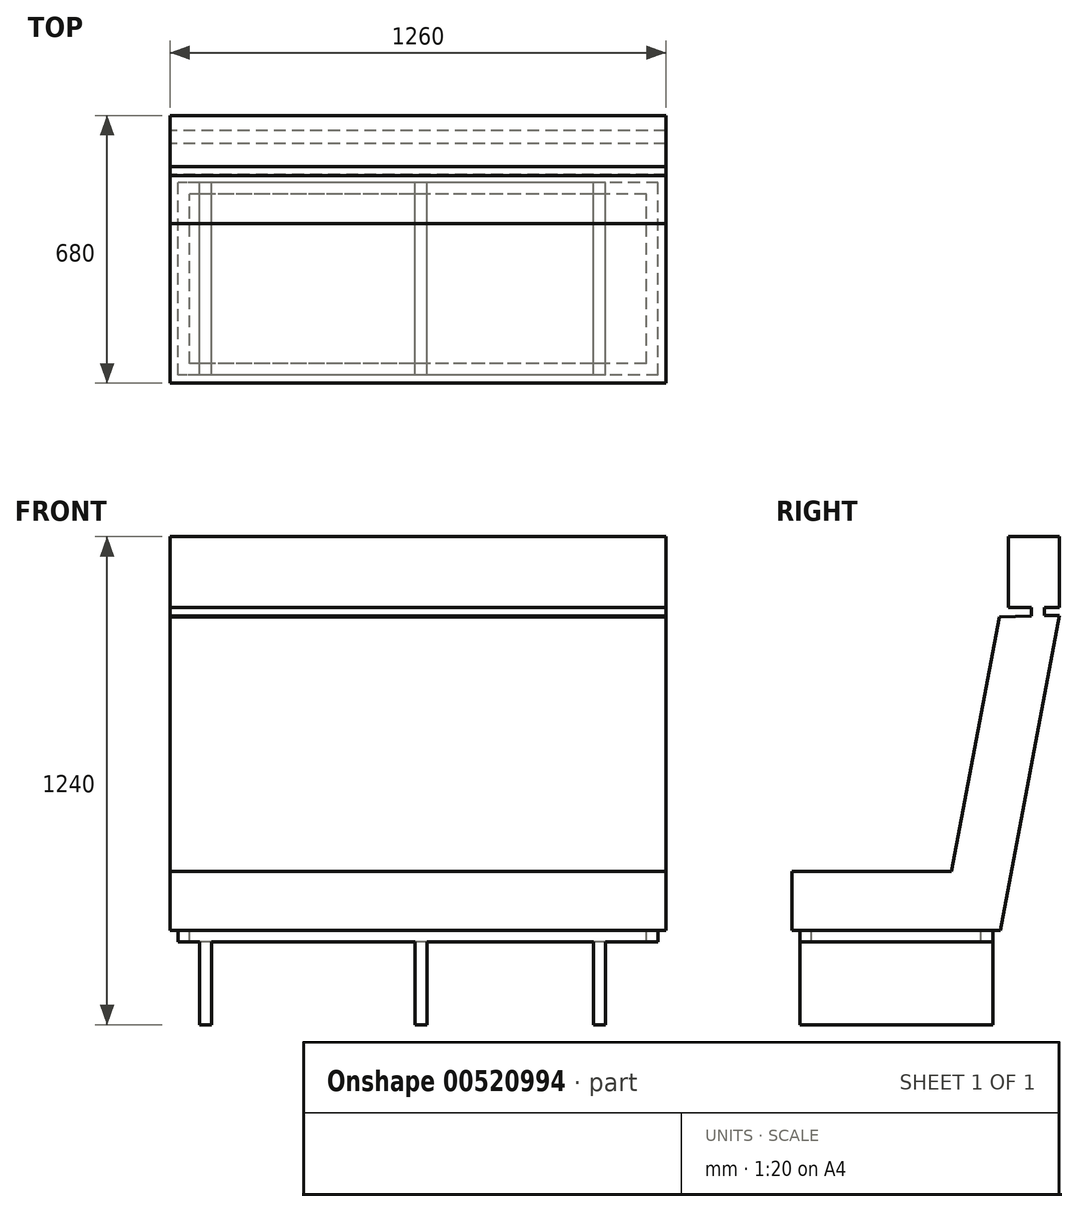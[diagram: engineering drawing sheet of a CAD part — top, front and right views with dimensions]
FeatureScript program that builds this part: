
annotation { "Feature Type Name" : "Feature", "Feature Type Description" : "" }
export const myFeature = defineFeature(function(context is Context, id is Id, definition is map)
    precondition{}
    {
        {
            var Q0;
            Q0=qCreatedBy(makeId("Right.planeOp"),FACE);
            var sketch = newSketch(context, id + "F0", { "sketchPlane" : qUnion([Q0])});
            skLineSegment(sketch, "E0", {"start": v(0, 0) * mm, "end": v(0, 800) * mm, "construction": true});
            skLineSegment(sketch, "E1", {"start": v(0, 0) * mm, "end": v(-150, 0) * mm, "construction": true});
            skLineSegment(sketch, "E2", {"start": v(-150, 0) * mm, "end": v(0, 800) * mm});
            skLineSegment(sketch, "E3", {"start": v(-150, 0) * mm, "end": v(-680, 0) * mm});
            skLineSegment(sketch, "E4.0", {"start": v(-274.49, 150) * mm, "end": v(-153.31, 796.27) * mm});
            skLineSegment(sketch, "E4.1", {"start": v(-274.49, 150) * mm, "end": v(-680, 150) * mm});
            skLineSegment(sketch, "E5", {"start": v(-680, 0) * mm, "end": v(-680, 150) * mm});
            skLineSegment(sketch, "E6", {"start": v(0, 800) * mm, "end": v(-38.22, 799.07) * mm});
            skLineSegment(sketch, "E7.bottom", {"start": v(0, 820) * mm, "end": v(-38.22, 820) * mm});
            skLineSegment(sketch, "E7.top", {"start": v(0, 1000) * mm, "end": v(-130, 1000) * mm});
            skLineSegment(sketch, "E7.left", {"start": v(0, 820) * mm, "end": v(0, 1000) * mm});
            skLineSegment(sketch, "E7.right", {"start": v(-130, 820) * mm, "end": v(-130, 1000) * mm});
            skLineSegment(sketch, "E8", {"start": v(-38.22, 820) * mm, "end": v(-38.22, 799.07) * mm});
            skLineSegment(sketch, "E9", {"start": v(-71.85, 798.25) * mm, "end": v(-71.85, 820) * mm});
            skLineSegment(sketch, "E10.trimOffspring", {"start": v(-71.85, 798.25) * mm, "end": v(-153.31, 796.27) * mm});
            skLineSegment(sketch, "E11.trimOffspring", {"start": v(-71.85, 820) * mm, "end": v(-130, 820) * mm});
            skSolve(sketch);
        }
        {
            var Q0;
            Q0 = qSketchRegion(id + "F0", true);
            extrude(context, id + "F1", {"entities" : qUnion([Q0]), "depth" : 1260 * mm, "offsetDistance" : 25 * mm});
        }
        {
            var Q0;
            Q0=makeQuery(id+"F1.opExtrude","SWEPT_FACE",FACE,{"disambiguationData":[OSD([sQuery(id+"F0.wireOp",EDGE,"E3")])]});
            var sketch = newSketch(context, id + "F2", { "sketchPlane" : qUnion([Q0])});
            skLineSegment(sketch, "E12.bottom", {"start": v(1260, 680) * mm, "end": v(0, 680) * mm, "construction": true});
            skLineSegment(sketch, "E12.top", {"start": v(1260, 150) * mm, "end": v(0, 150) * mm, "construction": true});
            skLineSegment(sketch, "E12.left", {"start": v(1260, 680) * mm, "end": v(1260, 150) * mm, "construction": true});
            skLineSegment(sketch, "E12.right", {"start": v(0, 680) * mm, "end": v(0, 150) * mm, "construction": true});
            skLineSegment(sketch, "E13.0", {"start": v(20, 660) * mm, "end": v(20, 170) * mm});
            skLineSegment(sketch, "E13.1", {"start": v(1240, 660) * mm, "end": v(20, 660) * mm});
            skLineSegment(sketch, "E13.2", {"start": v(1240, 660) * mm, "end": v(1240, 170) * mm});
            skLineSegment(sketch, "E13.3", {"start": v(1240, 170) * mm, "end": v(20, 170) * mm});
            skLineSegment(sketch, "E14.0", {"start": v(50, 630) * mm, "end": v(50, 200) * mm});
            skLineSegment(sketch, "E14.1", {"start": v(1210, 630) * mm, "end": v(50, 630) * mm});
            skLineSegment(sketch, "E14.2", {"start": v(1210, 630) * mm, "end": v(1210, 200) * mm});
            skLineSegment(sketch, "E14.3", {"start": v(1210, 200) * mm, "end": v(50, 200) * mm});
            skSolve(sketch);
        }
        {
            var Q0;
            Q0 = qSketchRegion(id + "F2", true);
            extrude(context, id + "F3", {"entities" : qUnion([Q0]), "operationType" : NewBodyOperationType.ADD, "depth" : 30 * mm, "offsetDistance" : 25 * mm});
        }
        {
            var Q0;
            Q0=makeQuery(id+"F3.opExtrude","CAP_FACE",FACE,{"disambiguationData":[OSD([sQuery(id+"F2.wireOp",EDGE,"E13.0"),sQuery(id+"F2.wireOp",EDGE,"E13.1"),sQuery(id+"F2.wireOp",EDGE,"E13.2"),sQuery(id+"F2.wireOp",EDGE,"E13.3"),sQuery(id+"F2.wireOp",EDGE,"E14.0"),sQuery(id+"F2.wireOp",EDGE,"E14.1"),sQuery(id+"F2.wireOp",EDGE,"E14.2"),sQuery(id+"F2.wireOp",EDGE,"E14.3")])],"isStart":false});
            var sketch = newSketch(context, id + "F4", { "sketchPlane" : qUnion([Q0])});
            skLineSegment(sketch, "E15.bottom", {"start": v(1105.84, 660) * mm, "end": v(1075.84, 660) * mm});
            skLineSegment(sketch, "E15.top", {"start": v(1105.84, 170) * mm, "end": v(1075.84, 170) * mm});
            skLineSegment(sketch, "E15.left", {"start": v(1105.84, 660) * mm, "end": v(1105.84, 170) * mm});
            skLineSegment(sketch, "E15.right", {"start": v(1075.84, 660) * mm, "end": v(1075.84, 170) * mm});
            skLineSegment(sketch, "E16.bottom", {"start": v(622.32, 660) * mm, "end": v(652.32, 660) * mm});
            skLineSegment(sketch, "E16.top", {"start": v(622.32, 170) * mm, "end": v(652.32, 170) * mm});
            skLineSegment(sketch, "E16.left", {"start": v(622.32, 660) * mm, "end": v(622.32, 170) * mm});
            skLineSegment(sketch, "E16.right", {"start": v(652.32, 660) * mm, "end": v(652.32, 170) * mm});
            skLineSegment(sketch, "E17.bottom", {"start": v(75.46, 660) * mm, "end": v(105.46, 660) * mm});
            skLineSegment(sketch, "E17.top", {"start": v(75.46, 170) * mm, "end": v(105.46, 170) * mm});
            skLineSegment(sketch, "E17.left", {"start": v(75.46, 660) * mm, "end": v(75.46, 170) * mm});
            skLineSegment(sketch, "E17.right", {"start": v(105.46, 660) * mm, "end": v(105.46, 170) * mm});
            skSolve(sketch);
        }
        {
            var Q0;
            Q0 = qSketchRegion(id + "F4", true);
            extrude(context, id + "F5", {"entities" : qUnion([Q0]), "operationType" : NewBodyOperationType.ADD, "depth" : 210 * mm, "offsetDistance" : 25 * mm});
        }
    });
